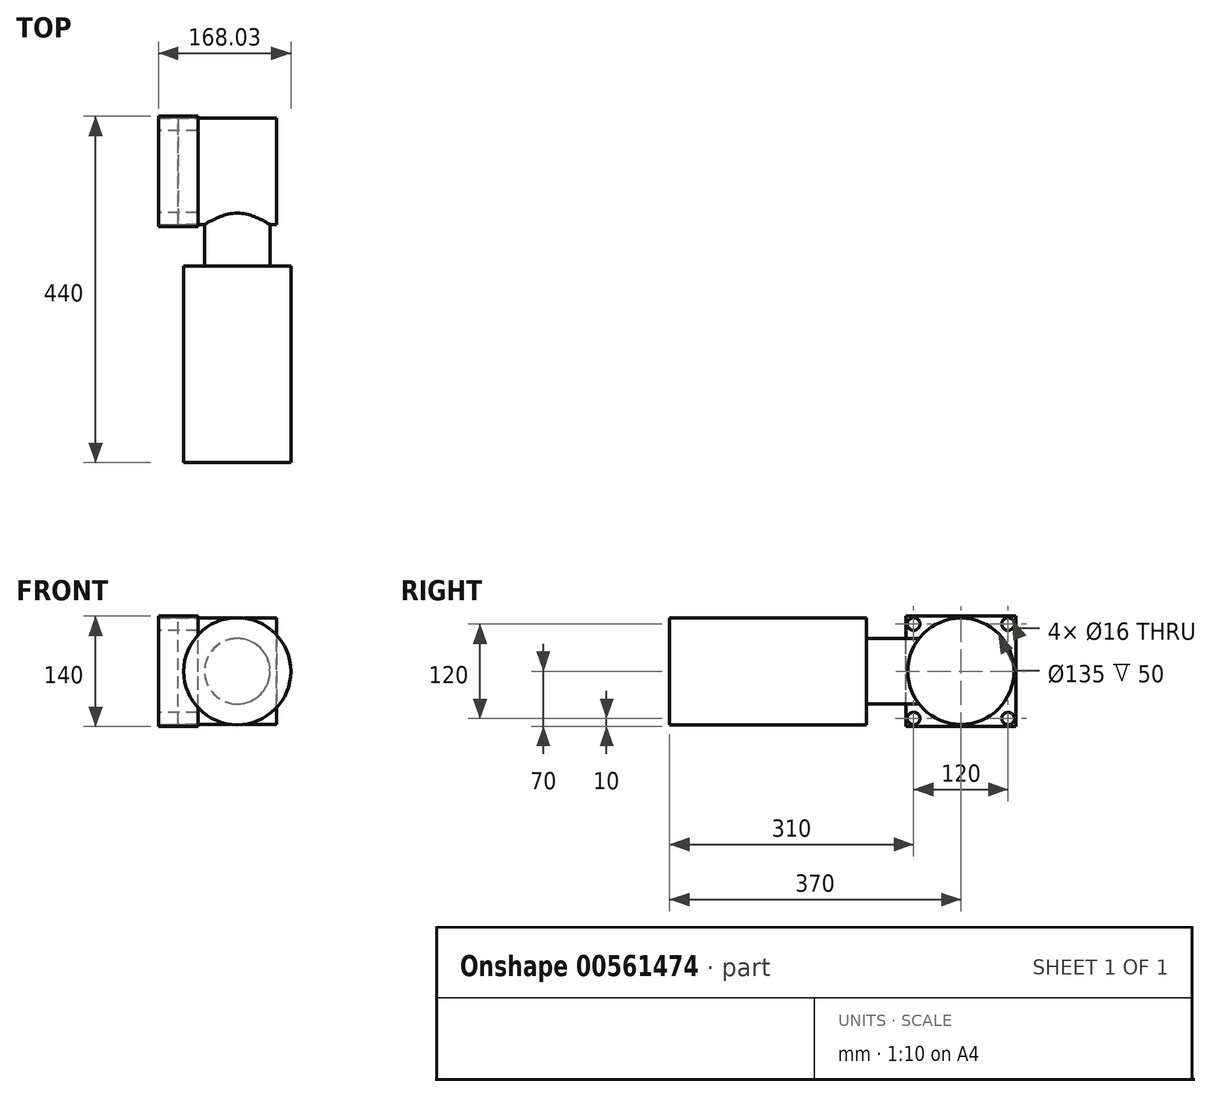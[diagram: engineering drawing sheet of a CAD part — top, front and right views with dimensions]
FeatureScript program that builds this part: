
annotation { "Feature Type Name" : "Feature", "Feature Type Description" : "" }
export const myFeature = defineFeature(function(context is Context, id is Id, definition is map)
    precondition{}
    {
        {
            var Q0;
            Q0=qCreatedBy(makeId("Right.planeOp"),FACE);
            var sketch = newSketch(context, id + "F0", { "sketchPlane" : qUnion([Q0])});
            skCircle(sketch, "E0", {"center": v(0, 0) * mm, "radius": 67.5 * mm});
            skLineSegment(sketch, "E1.bottom", {"start": v(70, -70) * mm, "end": v(-70, -70) * mm});
            skLineSegment(sketch, "E1.top", {"start": v(70, 70) * mm, "end": v(-70, 70) * mm});
            skLineSegment(sketch, "E1.left", {"start": v(70, -70) * mm, "end": v(70, 70) * mm});
            skLineSegment(sketch, "E1.right", {"start": v(-70, -70) * mm, "end": v(-70, 70) * mm});
            skSolve(sketch);
        }
        {
            var Q0;
            {var subQ0=sQuery(id+"F0.wireOp",EDGE,"E1.top");var subQ1=sQuery(id+"F0.wireOp",EDGE,"E0");var subQ2=makeQuery(id+"F0.imprint","INTERSECT",VERTEX,{"derivedFrom":[subQ1,subQ0]});Q0=makeQuery(id+"F0.imprint","IMPRINT",FACE,{"disambiguationData":[TD([[makeQuery(id+"F0.imprint","IMPRINT",EDGE,{"disambiguationData":[TD([[subQ2,-1.0]])],"derivedFrom":subQ1}),-1.0]])]});}
            var Q1;
            {var subQ0=sQuery(id+"F0.wireOp",EDGE,"E1.top");var subQ1=sQuery(id+"F0.wireOp",EDGE,"E0");var subQ2=makeQuery(id+"F0.imprint","INTERSECT",VERTEX,{"derivedFrom":[subQ1,subQ0]});Q1=makeQuery(id+"F0.imprint","IMPRINT",FACE,{"disambiguationData":[TD([[makeQuery(id+"F0.imprint","IMPRINT",EDGE,{"disambiguationData":[TD([[subQ2,1.0]])],"derivedFrom":subQ1}),-1.0]])]});}
            var Q2;
            {var subQ0=sQuery(id+"F0.wireOp",EDGE,"E1.left");var subQ1=sQuery(id+"F0.wireOp",EDGE,"E0");var subQ2=makeQuery(id+"F0.imprint","INTERSECT",VERTEX,{"derivedFrom":[subQ1,subQ0]});Q2=makeQuery(id+"F0.imprint","IMPRINT",FACE,{"disambiguationData":[TD([[makeQuery(id+"F0.imprint","IMPRINT",EDGE,{"disambiguationData":[TD([[subQ2,1.0]])],"derivedFrom":subQ1}),-1.0]])]});}
            var Q3;
            {var subQ0=sQuery(id+"F0.wireOp",EDGE,"E1.right");var subQ1=sQuery(id+"F0.wireOp",EDGE,"E0");var subQ2=makeQuery(id+"F0.imprint","INTERSECT",VERTEX,{"derivedFrom":[subQ1,subQ0]});Q3=makeQuery(id+"F0.imprint","IMPRINT",FACE,{"disambiguationData":[TD([[makeQuery(id+"F0.imprint","IMPRINT",EDGE,{"disambiguationData":[TD([[subQ2,-1.0]])],"derivedFrom":subQ1}),-1.0]])]});}
            extrude(context, id + "F1", {"entities" : qUnion([Q0, Q1, Q2, Q3]), "oppositeDirection" : true, "depth" : 50 * mm, "offsetDistance" : 25 * mm});
        }
        {
            var Q0;
            Q0=makeQuery(id+"F1.opExtrude","CAP_FACE",FACE,{"disambiguationData":[OSD([sQuery(id+"F0.wireOp",EDGE,"E0"),sQuery(id+"F0.wireOp",EDGE,"E1.bottom"),sQuery(id+"F0.wireOp",EDGE,"E1.top"),sQuery(id+"F0.wireOp",EDGE,"E1.left"),sQuery(id+"F0.wireOp",EDGE,"E1.right")])],"isStart":true});
            var sketch = newSketch(context, id + "F2", { "sketchPlane" : qUnion([Q0])});
            skSolve(sketch);
        }
        {
            var Q0;
            Q0=makeQuery(id+"F2.imprint","IMPRINT",FACE,{"disambiguationData":[TD([[makeQuery(id+"F2.imprint","IMPRINT",EDGE,{"derivedFrom":makeQuery(id+"F1.opExtrude","CAP_EDGE",EDGE,{"disambiguationData":[OSD([sQuery(id+"F0.wireOp",EDGE,"E0")])],"isStart":true})}),1.0]])]});
            extrude(context, id + "F3", {"entities" : qUnion([Q0]), "depth" : 100 * mm, "offsetDistance" : 25 * mm, "hasSecondDirection" : true, "secondDirectionOppositeDirection" : true, "secondDirectionDepth" : 25 * mm});
        }
        {
            var Q0;
            Q0=qCreatedBy(makeId("Front.planeOp"),FACE);
            var sketch = newSketch(context, id + "F4", { "sketchPlane" : qUnion([Q0])});
            skCircle(sketch, "E2", {"center": v(50, 0) * mm, "radius": 41.67 * mm});
            skSolve(sketch);
        }
        {
            var Q0;
            Q0 = qSketchRegion(id + "F4", true);
            extrude(context, id + "F5", {"entities" : qUnion([Q0]), "operationType" : NewBodyOperationType.ADD, "depth" : 120 * mm, "offsetDistance" : 25 * mm});
        }
        {
            var Q0;
            Q0=makeQuery(id+"F5.opExtrude","CAP_FACE",FACE,{"disambiguationData":[OSD([sQuery(id+"F4.wireOp",EDGE,"E2")])],"isStart":false});
            var sketch = newSketch(context, id + "F6", { "sketchPlane" : qUnion([Q0])});
            skCircle(sketch, "E3", {"center": v(50, 0) * mm, "radius": 68.03 * mm});
            skSolve(sketch);
        }
        {
            var Q0;
            Q0=makeQuery(id+"F6.imprint","IMPRINT",FACE,{"disambiguationData":[TD([[makeQuery(id+"F6.imprint","IMPRINT",EDGE,{"derivedFrom":sQuery(id+"F6.wireOp",EDGE,"E3")}),1.0]])]});
            extrude(context, id + "F7", {"entities" : qUnion([Q0]), "depth" : 250 * mm, "offsetDistance" : 25 * mm});
        }
        {
            var Q0;
            Q0 = qSketchRegion(id + "F4", true);
            var Q1;
            Q1=makeQuery(id+"F7.opExtrude","CAP_FACE",FACE,{"disambiguationData":[OSD([sQuery(id+"F4.wireOp",EDGE,"E2"),sQuery(id+"F6.wireOp",EDGE,"E3")])],"isStart":false});
            extrude(context, id + "F8", {"entities" : qUnion([Q0]), "operationType" : NewBodyOperationType.ADD, "endBound" : BoundingType.UP_TO_SURFACE, "depth" : 25 * mm, "endBoundEntityFace" : qUnion([Q1]), "offsetDistance" : 25 * mm});
        }
        {
            var Q0;
            Q0=makeQuery(id+"F3.opExtrude","CAP_FACE",FACE,{"disambiguationData":[OSD([sQuery(id+"F0.wireOp",EDGE,"E0")])],"isStart":true});
            var sketch = newSketch(context, id + "F9", { "sketchPlane" : qUnion([Q0])});
            skCircle(sketch, "E4", {"center": v(60, -60) * mm, "radius": 8 * mm});
            skCircle(sketch, "E5", {"center": v(-60, 60) * mm, "radius": 8 * mm});
            skCircle(sketch, "E6", {"center": v(60, 60) * mm, "radius": 8 * mm});
            skCircle(sketch, "E7", {"center": v(-60, -60) * mm, "radius": 8 * mm});
            skSolve(sketch);
        }
        {
            var Q0;
            Q0=makeQuery(id+"F9.imprint","IMPRINT",FACE,{"disambiguationData":[TD([[makeQuery(id+"F9.imprint","IMPRINT",EDGE,{"derivedFrom":sQuery(id+"F9.wireOp",EDGE,"E6")}),1.0]])]});
            var Q1;
            Q1=makeQuery(id+"F9.imprint","IMPRINT",FACE,{"disambiguationData":[TD([[makeQuery(id+"F9.imprint","IMPRINT",EDGE,{"derivedFrom":sQuery(id+"F9.wireOp",EDGE,"E5")}),1.0]])]});
            var Q2;
            Q2=makeQuery(id+"F9.imprint","IMPRINT",FACE,{"disambiguationData":[TD([[makeQuery(id+"F9.imprint","IMPRINT",EDGE,{"derivedFrom":sQuery(id+"F9.wireOp",EDGE,"E7")}),1.0]])]});
            var Q3;
            Q3=makeQuery(id+"F9.imprint","IMPRINT",FACE,{"disambiguationData":[TD([[makeQuery(id+"F9.imprint","IMPRINT",EDGE,{"derivedFrom":sQuery(id+"F9.wireOp",EDGE,"E4")}),1.0]])]});
            extrude(context, id + "F10", {"entities" : qUnion([Q0, Q1, Q2, Q3]), "operationType" : NewBodyOperationType.REMOVE, "endBound" : BoundingType.SYMMETRIC, "oppositeDirection" : true, "depth" : 50 * mm, "offsetDistance" : 25 * mm});
        }
    });
